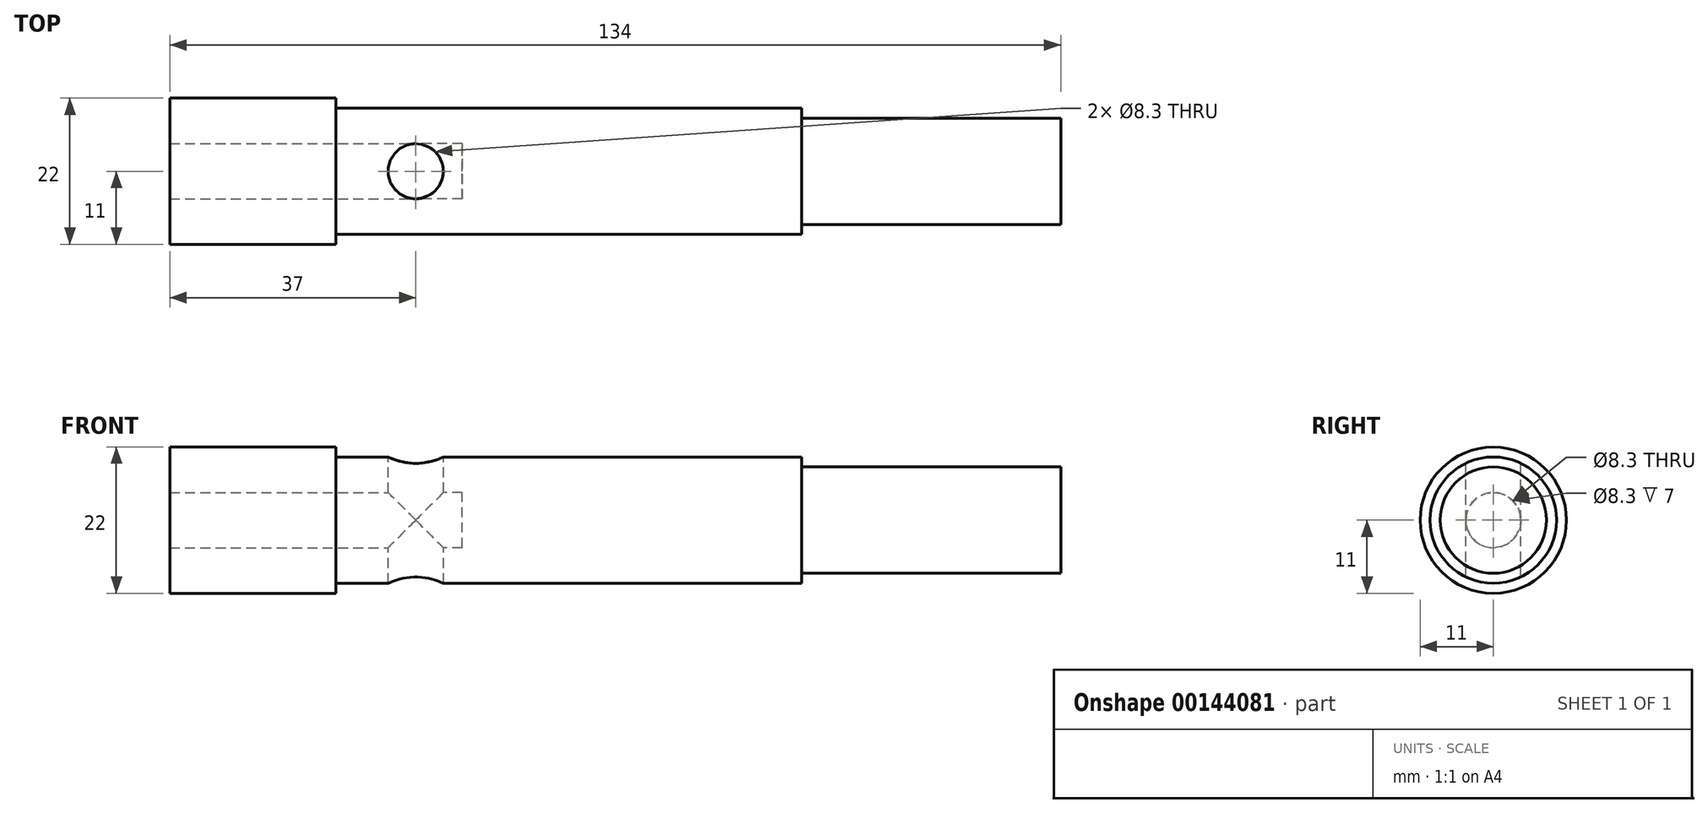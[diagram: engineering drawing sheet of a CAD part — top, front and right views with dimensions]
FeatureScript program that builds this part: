
annotation { "Feature Type Name" : "Feature", "Feature Type Description" : "" }
export const myFeature = defineFeature(function(context is Context, id is Id, definition is map)
    precondition{}
    {
        {
            var Q0;
            Q0=qCreatedBy(makeId("Right.planeOp"),FACE);
            var sketch = newSketch(context, id + "F0", { "sketchPlane" : qUnion([Q0])});
            skCircle(sketch, "E0", {"center": v(0, 0) * mm, "radius": 4.15 * mm});
            skCircle(sketch, "E1", {"center": v(0, 0) * mm, "radius": 11 * mm});
            skSolve(sketch);
        }
        {
            var Q0;
            Q0 = qSketchRegion(id + "F0", true);
            extrude(context, id + "F1", {"entities" : qUnion([Q0]), "oppositeDirection" : true, "depth" : 25 * mm});
        }
        {
            var Q0;
            Q0=makeQuery(id+"F1.opExtrude","CAP_FACE",FACE,{"disambiguationData":[OSD([sQuery(id+"F0.wireOp",EDGE,"E0"),sQuery(id+"F0.wireOp",EDGE,"E1")])],"isStart":true});
            var sketch = newSketch(context, id + "F2", { "sketchPlane" : qUnion([Q0])});
            skCircle(sketch, "E2", {"center": v(0, 0) * mm, "radius": 9.5 * mm});
            skSolve(sketch);
        }
        {
            var Q0;
            Q0 = qSketchRegion(id + "F2", true);
            extrude(context, id + "F3", {"entities" : qUnion([Q0]), "operationType" : NewBodyOperationType.ADD, "depth" : 70 * mm});
        }
        {
            var Q0;
            Q0=qCreatedBy(makeId("Origin.pointOp"),VERTEX);
            var Q1;
            Q1=qCreatedBy(makeId("Top.planeOp"),FACE);
            cPlane(context, id + "F4", {"entities" : qUnion([Q0, Q1]), "cplaneType" : CPlaneType.PLANE_POINT, "offset" : 25 * mm, "width" : 150 * mm, "height" : 150 * mm});
        }
        {
            var Q0;
            Q0=qCreatedBy(id+"F4.planeOp",FACE);
            var sketch = newSketch(context, id + "F5", { "sketchPlane" : qUnion([Q0])});
            skCircle(sketch, "E3", {"center": v(12, 0) * mm, "radius": 4.15 * mm});
            skSolve(sketch);
        }
        {
            var Q0;
            Q0 = qSketchRegion(id + "F5", true);
            extrude(context, id + "F6", {"entities" : qUnion([Q0]), "operationType" : NewBodyOperationType.REMOVE, "endBound" : BoundingType.THROUGH_ALL, "oppositeDirection" : true, "depth" : 25 * mm, "hasSecondDirection" : true, "secondDirectionBound" : SecondDirectionBoundingType.THROUGH_ALL, "secondDirectionOppositeDirection" : false, "secondDirectionDepth" : 25 * mm});
        }
        {
            var Q0;
            Q0=makeQuery(id+"F3.opExtrude","CAP_FACE",FACE,{"disambiguationData":[OSD([sQuery(id+"F2.wireOp",EDGE,"E2")])],"isStart":false});
            var sketch = newSketch(context, id + "F7", { "sketchPlane" : qUnion([Q0])});
            skCircle(sketch, "E4", {"center": v(0, 0) * mm, "radius": 8 * mm});
            skSolve(sketch);
        }
        {
            var Q0;
            Q0 = qSketchRegion(id + "F7", true);
            extrude(context, id + "F8", {"entities" : qUnion([Q0]), "operationType" : NewBodyOperationType.ADD, "depth" : 39 * mm});
        }
        {
            var Q0;
            Q0=makeQuery(id+"F3.opExtrude","CAP_FACE",FACE,{"disambiguationData":[OSD([sQuery(id+"F2.wireOp",EDGE,"E2")])],"isStart":true});
            extrude(context, id + "F9", {"entities" : qUnion([Q0]), "operationType" : NewBodyOperationType.REMOVE, "oppositeDirection" : true, "depth" : 19 * mm});
        }
    });
